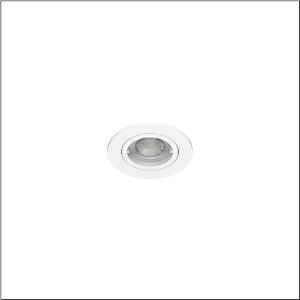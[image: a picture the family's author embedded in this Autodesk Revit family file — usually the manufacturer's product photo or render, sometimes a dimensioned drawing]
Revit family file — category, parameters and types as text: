
# Revit family: lunis_41_spot_51dt137a41a
name_source: partatom
category: Lighting Fixtures
units: mm (PartAtom-declared; Revit-internal decimal feet)

## family parameters
Cut with Voids When Loaded = No
Host = Face
Light Source = No
Part Type = Normal
Room Calculation Point = No
Round Connector Dimension = Use Diameter
Shared = No

## types (1)
- Lunis 41 Spot (1 x LED, 550 lm, 5 W, 4000K)
    Apparent Load = 5 VA
    CIE Flux Codes = 87 97 99 100 100
    Color Rendering = 80
    Color Temperature = 4000K
    Default Elevation = 1800 mm
    Description = Lunis 41,  Spot, downlight, light emission: direct distribution, LED rated luminous flux: 550lm, light colour: 840, control gear: ECG, mains connection: 230V, AC, 50/60Hz, housing, round, of aluminium, coated, traffic white (RAL 9016), diameter: 88mm, recess depth: 54mm, protection rating (complete): IP20, protection rating (on room side): IP20, insulation class (complete): insulation class II (safety insulation), certification: CE, permissible ambient temperature for indoor applications: -20..+40°C, packaging unit: 1 piece
    Height = 0 mm  [stored 0 ft]
    Lamp = 1 x LED
    Lamp Light Flux = 550 lm
    Lamp Power = 5 W
    Lamp count = 1
    Length = 88 mm
    Luminous efficacy = 110 lm/W
    Manufacturer = Siteco
    ModVariant = No
    Model = 51DT137A41A
    Mounting Place = Ceiling
    Mounting Type = Recessed
    Number of Poles = 1
    OnlyDefault = Yes
    Power Factor = 1
    Product Name = Lunis 41 Spot
    Product group = downlight
    ProductGroupID = 400
    Protection Class = Protection class II
    Protection Degree = IP 20
    RLX_Detail_Level = 1
    RLX_Emergency_Light_Flux = 0 lm
    RLX_Emergency_Type = 0
    RLX_Emergency_Type_DB = No
    RlxData = <blob elided: 37985 chars, md5=ff1523f1>
    Socket = socket
    Standby Power = 0 W
    System Light Flux = 550 lm
    System Power = 5 W
    Type Comments = Product without accessories
    Type Image = l_1005286.jpg
    URL = http://relux.com
    VarID = ---
    Voltage = 0 V
    Weight = 0.00 kg
    Width = 0 mm  [stored 0 ft]

note: [stored X ft] marks values corroborated as IEEE doubles in the binary element streams (Revit-internal decimal feet)

## geometry (parser evidence)
native form markers: Blend x4, Sweep x10
no freeform markers — native parametric forms only
